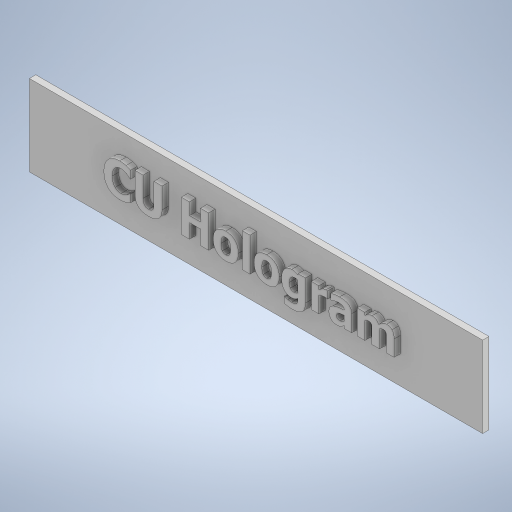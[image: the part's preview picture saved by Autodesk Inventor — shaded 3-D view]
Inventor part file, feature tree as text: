
AUTODESK INVENTOR PART (.ipt)
format: ipt  version: 2024 (Build 280153000, 153)  size: 487,936 bytes
history: native  units: mm
features: plane x2, extrude x2, sketch x2
ambient origin geometry x8: Origin, YZ Plane, XZ Plane, XY Plane, X Axis, Y Axis, Z Axis, Center Point
bodies: Solid1 (feature_tree)
feature tree (6):
  plane  "Work Plane4"
  extrude  "Decoration Plate"  Depth=25.4mm
  plane  "Work Plane3"
  extrude  "Decoration Text"  TaperAngle=0.0deg  [1 undecoded]
  sketch  "Sketch7"  dims[d36=12.7mm d37=25.4mm]
  sketch  "Sketch8"  dims[d38=5.0mm d39=0.0mm d40=0.0mm d41=0.0mm d42=0.0mm d43=0.0mm d44=5.0mm d45=0.0mm]
note: 1 required parameter value undecoded (feature->parameter linkage not recoverable at this tier; creation-order binding heuristic only, values carry confidence <= 0.55)
